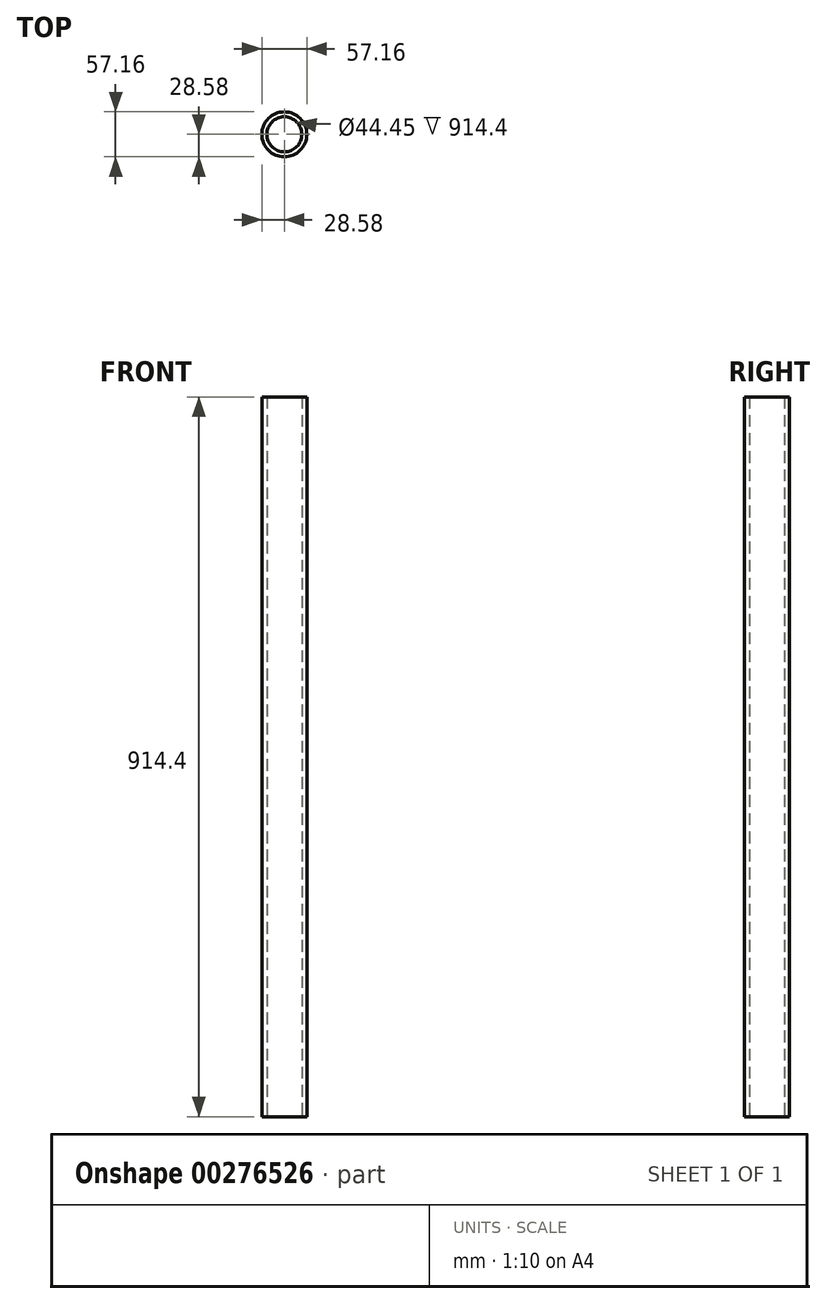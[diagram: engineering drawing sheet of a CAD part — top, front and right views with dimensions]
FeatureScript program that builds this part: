
annotation { "Feature Type Name" : "Feature", "Feature Type Description" : "" }
export const myFeature = defineFeature(function(context is Context, id is Id, definition is map)
    precondition{}
    {
        {
            var Q0;
            Q0=qCreatedBy(makeId("Top.planeOp"),FACE);
            var sketch = newSketch(context, id + "F0", { "sketchPlane" : qUnion([Q0])});
            skCircle(sketch, "E0", {"center": v(0, 0) * mm, "radius": 22.23 * mm});
            skCircle(sketch, "E1.0", {"center": v(0, 0) * mm, "radius": 28.58 * mm});
            skSolve(sketch);
        }
        {
            var Q0;
            Q0=makeQuery(id+"F0.imprint","IMPRINT",FACE,{"disambiguationData":[TD([[makeQuery(id+"F0.imprint","IMPRINT",EDGE,{"derivedFrom":sQuery(id+"F0.wireOp",EDGE,"E0")}),-1.0]])]});
            var Q1;
            Q1=sQuery(id+"F0.wireOp",EDGE,"E1.0");
            extrude(context, id + "F1", {"entities" : qUnion([Q0]), "surfaceEntities" : qUnion([Q1]), "depth" : 914.4 * mm});
        }
    });
